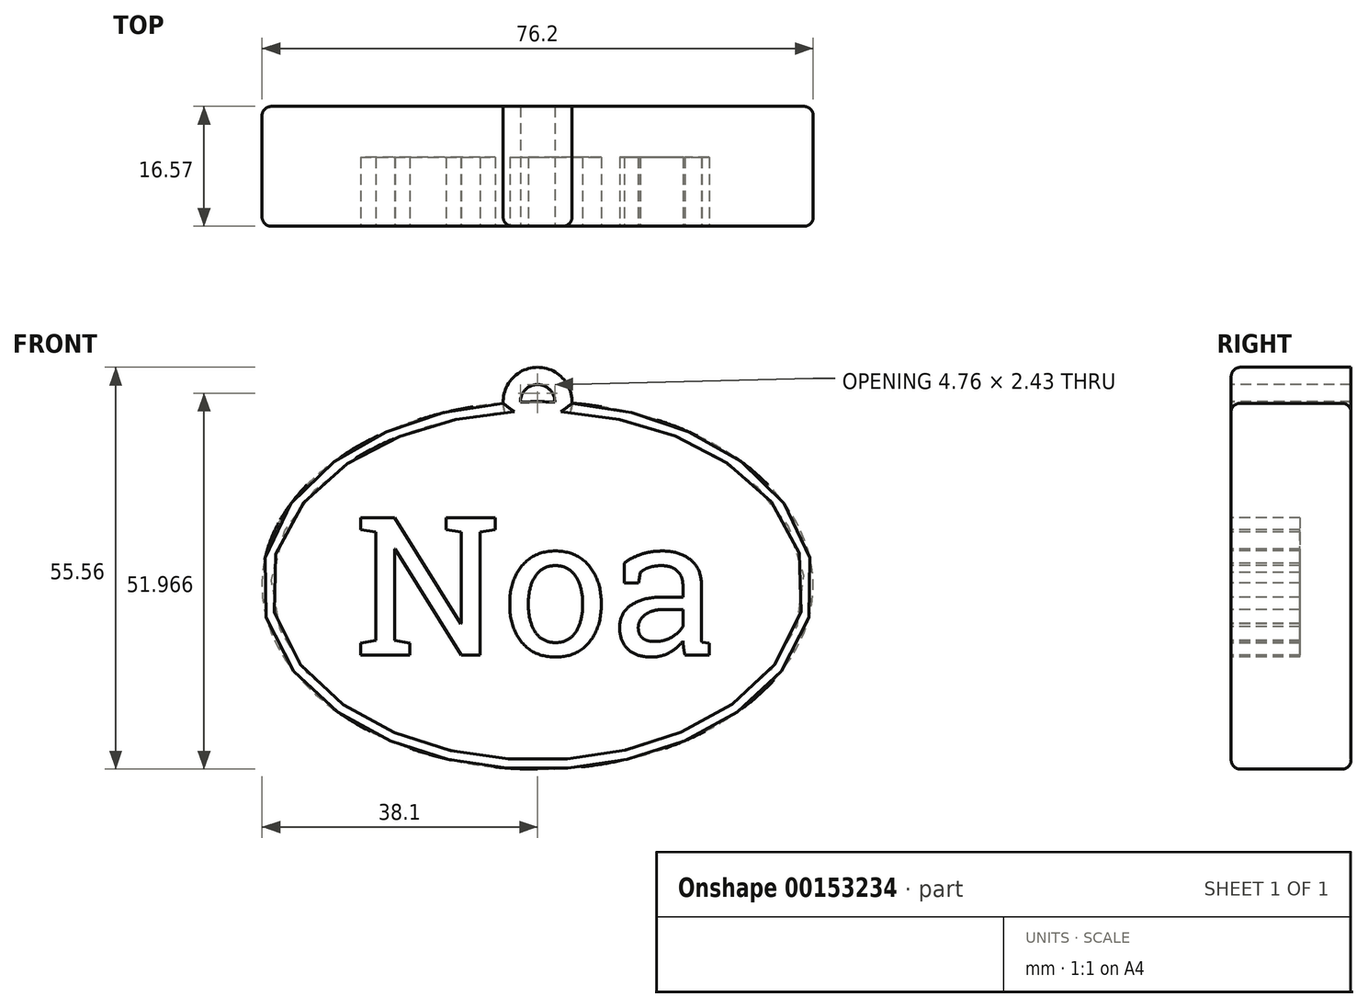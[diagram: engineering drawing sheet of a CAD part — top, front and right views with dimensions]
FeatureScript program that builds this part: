
annotation { "Feature Type Name" : "Feature", "Feature Type Description" : "" }
export const myFeature = defineFeature(function(context is Context, id is Id, definition is map)
    precondition{}
    {
        {
            var Q0;
            Q0=qCreatedBy(makeId("Front.planeOp"),FACE);
            var sketch = newSketch(context, id + "F0", { "sketchPlane" : qUnion([Q0])});
            skEllipse(sketch, "E0", {"center": v(0, 0) * mm, "majorRadius": 38.1 * mm, "minorRadius": 25.4 * mm, "majorAxis": v(1, 0)});
            skSolve(sketch);
        }
        {
            assignVariable(context, id + "F1", {"name" : "Nametag_Height", "anyValue" : 19.05 * mm});
        }
        {
            var Q0;
            Q0=makeQuery(id+"F0.imprint","IMPRINT",FACE,{"disambiguationData":[TD([[makeQuery(id+"F0.imprint","IMPRINT",EDGE,{"derivedFrom":sQuery(id+"F0.wireOp",EDGE,"E0")}),1.0]])]});
            extrude(context, id + "F2", {"entities" : qUnion([Q0]), "depth" : 16.57 * mm});
        }
        {
            var Q0;
            Q0=makeQuery(id+"F2.opExtrude","CAP_FACE",FACE,{"disambiguationData":[OSD([sQuery(id+"F0.wireOp",EDGE,"E0")])],"isStart":false});
            var sketch = newSketch(context, id + "F3", { "sketchPlane" : qUnion([Q0])});
            skText(sketch, "E1", { "text": "Noa", "fontName": "RobotoSlab-Regular.ttf"});
            skPoint(sketch, "E2.0", {"position": v(0, 0) * mm});
            const initialGuessF3  = {"E1": [-0.0254, -0.00963, 1, 0, 0.01926]};
            skSetInitialGuess(sketch, initialGuessF3);
            skSolve(sketch);
        }
        {
            var Q0;
            Q0 = qSketchRegion(id + "F3", true);
            extrude(context, id + "F4", {"entities" : qUnion([Q0]), "operationType" : NewBodyOperationType.REMOVE, "oppositeDirection" : true, "depth" : getVariable(context, 'Nametag_Height') / 2});
        }
        {
            var Q0;
            {var subQ0=sQuery(id+"F0.wireOp",EDGE,"E0");Q0=makeQuery(id+"F4.boolean.opBoolean","SPLIT",FACE,{"disambiguationData":[TD([makeQuery(id+"F2.opExtrude","SWEPT_FACE",FACE,{"disambiguationData":[OSD([subQ0])]})])],"derivedFrom":makeQuery(id+"F2.opExtrude","CAP_FACE",FACE,{"disambiguationData":[OSD([subQ0])],"isStart":false})});}
            var sketch = newSketch(context, id + "F5", { "sketchPlane" : qUnion([Q0])});
            skCircle(sketch, "E3", {"center": v(0, 25.4) * mm, "radius": 2.38 * mm});
            skCircle(sketch, "E4", {"center": v(0, 25.4) * mm, "radius": 4.76 * mm});
            skSolve(sketch);
        }
        {
            var Q0;
            {var subQ0=sQuery(id+"F5.wireOp",EDGE,"E3");var subQ1=makeQuery(id+"F2.opExtrude","CAP_EDGE",EDGE,{"disambiguationData":[OSD([sQuery(id+"F0.wireOp",EDGE,"E0")])],"isStart":false});var subQ2=makeQuery(id+"F5.imprint","INTERSECT",VERTEX,{"disambiguationData":[OD(0.0)],"derivedFrom":[subQ1,subQ0]});Q0=makeQuery(id+"F5.imprint","IMPRINT",FACE,{"disambiguationData":[TD([[makeQuery(id+"F5.imprint","IMPRINT",EDGE,{"disambiguationData":[TD([[subQ2,1.0]])],"derivedFrom":subQ0}),-1.0]])]});}
            var Q1;
            Q1=makeQuery(id+"F2.opExtrude","CAP_FACE",FACE,{"disambiguationData":[OSD([sQuery(id+"F0.wireOp",EDGE,"E0")])],"isStart":true});
            extrude(context, id + "F6", {"entities" : qUnion([Q0]), "operationType" : NewBodyOperationType.ADD, "endBound" : BoundingType.UP_TO_SURFACE, "oppositeDirection" : true, "endBoundEntityFace" : qUnion([Q1]), "depth" : 25.4 * mm});
        }
        {
            var Q0;
            {var subQ0=sQuery(id+"F0.wireOp",EDGE,"E0");var subQ1=sQuery(id+"F5.wireOp",EDGE,"E4");Q0=makeQuery(id+"F6.boolean.opBoolean","SPLIT",EDGE,{"disambiguationData":[TD([makeQuery(id+"F6.opExtrude","SWEPT_FACE",FACE,{"disambiguationData":[OSD([subQ1])]})])],"derivedFrom":makeQuery(id+"F2.opExtrude","CAP_EDGE",EDGE,{"disambiguationData":[OSD([subQ0])],"isStart":false})});}
            var Q1;
            Q1=makeQuery(id+"F6.opExtrude","CAP_EDGE",EDGE,{"disambiguationData":[OSD([sQuery(id+"F5.wireOp",EDGE,"E4")])],"isStart":true});
            var Q2;
            {var subQ0=sQuery(id+"F5.wireOp",EDGE,"E4");var subQ1=sQuery(id+"F0.wireOp",EDGE,"E0");var subQ2=makeQuery(id+"F2.opExtrude","CAP_EDGE",EDGE,{"disambiguationData":[OSD([subQ1])],"isStart":false});Q2=makeQuery(id+"F6.opExtrude","TWEAK_EDGE",EDGE,{"derivedFrom":[makeQuery(id+"F2.opExtrude","CAP_FACE",FACE,{"disambiguationData":[OSD([subQ1])],"isStart":true}),makeQuery(id+"F5.imprint","IMPRINT",EDGE,{"disambiguationData":[TD([[makeQuery(id+"F5.imprint","INTERSECT",VERTEX,{"disambiguationData":[OD(0.0)],"derivedFrom":[subQ2,subQ0]}),1.0]])],"derivedFrom":subQ0})]});}
            var Q3;
            {var subQ0=sQuery(id+"F0.wireOp",EDGE,"E0");Q3=makeQuery(id+"F6.boolean.opBoolean","SPLIT",EDGE,{"disambiguationData":[TD([makeQuery(id+"F6.opExtrude","SWEPT_FACE",FACE,{"disambiguationData":[OSD([sQuery(id+"F5.wireOp",EDGE,"E4")])]})])],"derivedFrom":makeQuery(id+"F2.opExtrude","CAP_EDGE",EDGE,{"disambiguationData":[OSD([subQ0])],"isStart":true})});}
            fillet(context, id + "F7", {"entities" : qUnion([Q0, Q1, Q2, Q3]), "radius" : 1.27 * mm, "tangentPropagation" : true, "allowEdgeOverflow" : false});
        }
    });
